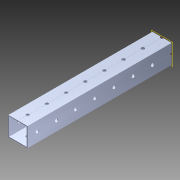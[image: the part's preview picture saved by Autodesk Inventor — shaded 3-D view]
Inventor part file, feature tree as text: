
AUTODESK INVENTOR PART (.ipt)
format: ipt  version: 2014 (Build 180170000, 170)  size: 1,171,968 bytes
history: native  units: in
note: dims shown in document units (in); Inventor stores cm internally (conversion verified against a paired STEP export)
features: pattern_circular x1, other x1, plane x1, extrude x1, imported_body x1, sketch x1
ambient origin geometry x8: Origin, YZ Plane, XZ Plane, XY Plane, X Axis, Y Axis, Z Axis, Center Point
bodies: Body1 (feature_tree)
feature tree (6):
  pattern_circular  "CirPattern2"
  other  "217-3426-STEP1"
  plane  "Work Plane1"
  extrude  "Extrusion1"  Depth=3937.0079in TaperAngle=0.0deg
  imported_body  "Base1"
  sketch  "Sketch1"  dims[d0=-7.5in d1=3937.0079in d2=0.0in]
